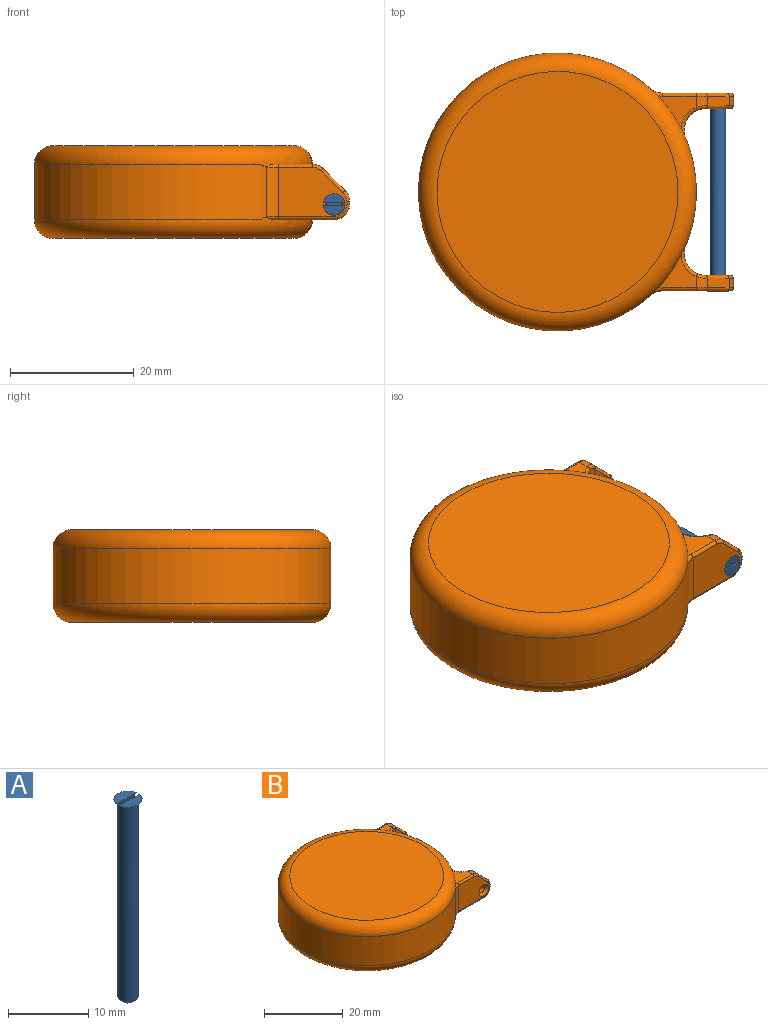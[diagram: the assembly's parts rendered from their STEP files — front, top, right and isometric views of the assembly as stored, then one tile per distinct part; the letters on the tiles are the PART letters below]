
ASSEMBLY  parts=2 mates=1
PART A: 9 faces, bbox 3.5x3.5x30.6 mm
  f0: plane 3.46x1.5mm, normal (0,0,1), area 3.9mm2, adj f2,f8
  f1: plane 3.46x1.5mm, normal (0,0,1), area 3.9mm2, adj f2,f7
  f2: cone r=1.03mm half-angle=45deg, axis (0,0,1), area 6.1mm2, adj f0,f1,f3,f6,f7,f8
  f3: cylinder r=1.25mm len=29.62mm, axis (0,0,1), area 232.6mm2, adj f2,f5
  f4: plane 1.5x1.5mm, normal (0,0,-1), area 1.8mm2, adj f5
  f5: cone r=1.25mm half-angle=45deg, axis (0,0,1), area 4.4mm2, adj f3,f4
  f6: plane 2.7x0.5mm, normal (0,0,1), area 1.3mm2, adj f2,f7,f8
  f7: plane 3.47x0.41mm, normal (0,1,0), area 1.2mm2, adj f1,f2,f6
  f8: plane 3.47x0.41mm, normal (0,-1,0), area 1.2mm2, adj f0,f2,f6
PART B: 73 faces, bbox 53.1x48.7x15 mm
  f0: plane 1.5x0.46mm, normal (1,0,0), area 0.7mm2, adj f19,f21,f37,f55
  f1: plane 9.78x5.3mm, normal (0,0,-1), area 21.1mm2, adj f6,f22,f48,f49,f66,f67
  f2: plane 6.24x5.3mm, normal (0,0,1), area 15.6mm2, adj f7,f18,f41,f59,f60
  f3: cylinder r=22.5mm len=45mm, axis (0,0,-1), area 930.2mm2, adj f6,f7,f30,f31,f50,f58,f59,f67
  f4: plane 39x39mm, normal (0,0,1), area 1194.6mm2, adj f7
  f5: plane 39x39mm, normal (0,0,-1), area 1194.6mm2, adj f6
  f6: torus R=19.5mm, axis (0,0,1), area 636.3mm2, adj f1,f3,f5,f10,f27,f40,f49,f58
  f7: torus R=19.5mm, axis (0,0,1), area 636.3mm2, adj f2,f3,f4,f8,f27,f32,f41,f50
  f8: plane 6.24x5.3mm, normal (0,0,1), area 15.6mm2, adj f7,f20,f32,f50,f51
  f9: plane 10.99x8mm, normal (0,-1,0), area 66.2mm2, adj f26,f30,f60,f61,f62,f63,f64,f65
  f10: plane 9.78x5.3mm, normal (0,0,-1), area 21.1mm2, adj f6,f21,f39,f40,f57,f58
  f11: plane 10.99x8mm, normal (0,1,0), area 75.8mm2, adj f31,f51,f52,f53,f54,f55,f56,f57
  f12: plane 1.5x0.46mm, normal (1,0,0), area 0.7mm2, adj f17,f22,f46,f64
  f13: plane 7.29x4mm, normal (0,1,0), area 16.9mm2, adj f25,f28,f44,f45,f46,f47,f48
  f14: plane 7.29x4mm, normal (0,-1,0), area 16.9mm2, adj f24,f29,f35,f36,f37,f38,f39
  f15: plane 3.54x3.54mm, normal (0.71,0,0.71), area 7.5mm2, adj f19,f20,f34,f35,f53
  f16: plane 3.54x3.54mm, normal (0.71,0,0.71), area 7.5mm2, adj f17,f18,f43,f44,f62
  f17: cylinder r=2.5mm len=1.77mm, axis (0,1,0), area 2.9mm2, adj f12,f16,f45,f63
  f18: cylinder r=2.5mm len=1.81mm, axis (0,-1,0), area 3.2mm2, adj f2,f16,f42,f61
  f19: cylinder r=2.5mm len=1.77mm, axis (0,1,0), area 2.9mm2, adj f0,f15,f36,f54
  f20: cylinder r=2.5mm len=1.81mm, axis (0,-1,0), area 3.2mm2, adj f8,f15,f33,f52
  f21: cylinder r=2.5mm len=2.5mm, axis (0,-1,0), area 5.9mm2, adj f0,f10,f38,f56
  f22: cylinder r=2.5mm len=2.5mm, axis (0,-1,0), area 5.9mm2, adj f1,f12,f47,f65
  f23: cone r=0mm half-angle=59deg, axis (0,-1,0), area 3.9mm2, adj f24
  f24: cylinder r=1.03mm len=2.05mm, axis (0,-1,0), area 9.7mm2, adj f14,f23
  f25: cylinder r=1.03mm len=2.05mm, axis (0,-1,0), area 11.4mm2, adj f13,f26
  f26: cone r=1.03mm half-angle=45deg, axis (0,-1,0), area 8.9mm2, adj f9,f25
  f27: cylinder r=22.5mm len=17.31mm, axis (0,0,-1), area 158.1mm2, adj f6,f7,f28,f29,f32,f40,f41,f49
  f28: cylinder r=3.5mm len=8mm, axis (0,0,-1), area 54.7mm2, adj f13,f27,f41,f42,f43,f49
  f29: cylinder r=3.5mm len=8mm, axis (0,0,-1), area 54.7mm2, adj f14,f27,f32,f33,f34,f40
  f30: cylinder r=3mm len=8mm, axis (0,0,-1), area 17.5mm2, adj f3,f9,f59,f67
  f31: cylinder r=3mm len=8mm, axis (0,0,-1), area 17.5mm2, adj f3,f11,f50,f58
  f32: torus R=4mm, axis (0,0,1), area 3.8mm2, adj f7,f8,f27,f29,f33
  f33: bspline ~2.5x1.23mm, area 1.3mm2, adj f20,f29,f32,f34
  f34: bspline ~1.74x1.66mm, area 0.1mm2, adj f15,f29,f33,f35
  f35: cylinder r=0.5mm len=3.77mm, axis (-0.71,0,0.71), area 3.8mm2, adj f14,f15,f34,f36
  f36: torus R=2mm, axis (0,1,0), area 1.4mm2, adj f14,f19,f35,f37
  f37: cylinder r=0.5mm len=0.5mm, axis (0,0,1), area 0.4mm2, adj f0,f14,f36,f38
  f38: torus R=2mm, axis (0,1,0), area 2.9mm2, adj f14,f21,f37,f39
  f39: cylinder r=0.5mm len=2mm, axis (-1,0,0), area 1.6mm2, adj f10,f14,f38,f40
  f40: torus R=4mm, axis (0,0,1), area 5mm2, adj f6,f10,f27,f29,f39
  f41: torus R=4mm, axis (0,0,1), area 3.8mm2, adj f2,f7,f27,f28,f42
  f42: bspline ~2.7x1.45mm, area 1.3mm2, adj f18,f28,f41,f43
  f43: bspline ~1.74x1.66mm, area 0.1mm2, adj f16,f28,f42,f44
  f44: cylinder r=0.5mm len=3.77mm, axis (-0.71,0,0.71), area 3.8mm2, adj f13,f16,f43,f45
  f45: torus R=2mm, axis (0,1,0), area 1.4mm2, adj f13,f17,f44,f46
  f46: cylinder r=0.5mm len=0.5mm, axis (0,0,-1), area 0.4mm2, adj f12,f13,f45,f47
  f47: torus R=2mm, axis (0,1,0), area 2.9mm2, adj f13,f22,f46,f48
  f48: cylinder r=0.5mm len=2mm, axis (1,0,0), area 1.6mm2, adj f1,f13,f47,f49
  f49: torus R=4mm, axis (0,0,1), area 5mm2, adj f1,f6,f27,f28,f48
  f50: torus R=3.5mm, axis (0,0,1), area 1.1mm2, adj f3,f7,f8,f31,f51
  f51: cylinder r=0.5mm len=5.46mm, axis (-1,0,0), area 4.3mm2, adj f8,f11,f50,f52
  f52: torus R=2mm, axis (0,1,0), area 1.4mm2, adj f11,f20,f51,f53
  f53: cylinder r=0.5mm len=3.89mm, axis (-0.71,0,0.71), area 3.9mm2, adj f11,f15,f52,f54
  f54: torus R=2mm, axis (0,1,0), area 1.4mm2, adj f11,f19,f53,f55
  f55: cylinder r=0.5mm len=0.5mm, axis (0,0,-1), area 0.4mm2, adj f0,f11,f54,f56
  f56: torus R=2mm, axis (0,1,0), area 2.9mm2, adj f11,f21,f55,f57
  f57: cylinder r=0.5mm len=8.99mm, axis (1,0,0), area 7.1mm2, adj f10,f11,f56,f58
  f58: torus R=3.5mm, axis (0,0,1), area 1.1mm2, adj f3,f6,f10,f31,f57
  f59: torus R=3.5mm, axis (0,0,1), area 1.1mm2, adj f2,f3,f7,f30,f60
  f60: cylinder r=0.5mm len=5.46mm, axis (1,0,0), area 4.3mm2, adj f2,f9,f59,f61
  f61: torus R=2mm, axis (0,1,0), area 1.4mm2, adj f9,f18,f60,f62
  f62: cylinder r=0.5mm len=3.89mm, axis (-0.71,0,0.71), area 3.9mm2, adj f9,f16,f61,f63
  f63: torus R=2mm, axis (0,1,0), area 1.4mm2, adj f9,f17,f62,f64
  f64: cylinder r=0.5mm len=0.5mm, axis (0,0,1), area 0.4mm2, adj f9,f12,f63,f65
  f65: torus R=2mm, axis (0,1,0), area 2.9mm2, adj f9,f22,f64,f66
  f66: cylinder r=0.5mm len=8.99mm, axis (-1,0,0), area 7.1mm2, adj f1,f9,f65,f67
  f67: torus R=3.5mm, axis (0,0,1), area 1.1mm2, adj f1,f3,f6,f30,f66
  f68: plane 39x39mm, normal (0,0,-1), area 1194.6mm2, adj f71
  f69: plane 39x39mm, normal (0,0,1), area 1194.6mm2, adj f70
  f70: torus R=19.5mm, axis (0,0,1), area 97.8mm2, adj f69,f72
  f71: torus R=19.5mm, axis (0,0,1), area 97.8mm2, adj f68,f72
  f72: cylinder r=20mm len=40mm, axis (0,0,-1), area 1131mm2, adj f70,f71
PLACE A rot(axis=(1,0,0),90deg) t=(10.8,-19.27,4.56)mm
PLACE B t=(-15.2,-3.25,-0.94)mm
MATE fastened A.f3 <-> B.f21  axis (0,-1,0) through (10.8,-18.77,4.56)mm
